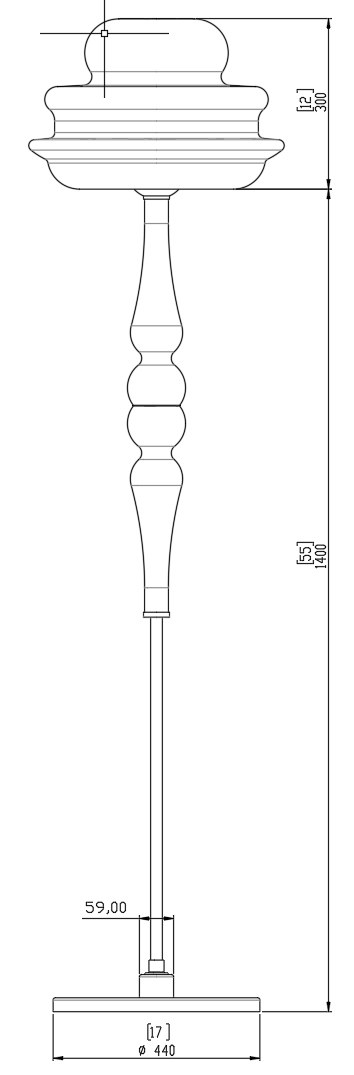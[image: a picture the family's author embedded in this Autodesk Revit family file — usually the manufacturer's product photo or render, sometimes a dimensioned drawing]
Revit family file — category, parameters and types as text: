
# Revit family: PEGGY-Floor
name_source: partatom
category: Lighting Fixtures
units: mm (PartAtom-declared; Revit-internal decimal feet)

## family parameters
Always vertical = Yes
Cut with Voids When Loaded = No
Light Source = No
OmniClass Number = 23.80.70.00
OmniClass Title = Lighting
Part Type = Normal
Room Calculation Point = No
Round Connector Dimension = Use Diameter
Shared = No
Work Plane-Based = Yes

## types (1)
- PEGGY PT
    Bulb Diametr = 15 mm  [stored 0.0492126 ft]
    Country = Europe
    Default Elevation = 1219 mm
    Depth = 28 mm
    Description = FLOOR LAMP
    Designer = Hangar Design Group
    Height = 1400 mm  [stored 4.59318 ft]
    Manufacturer = Vistosi
    Manufacturer country = Italy
    Model = PEGGY
    Type Comments = Hangar Design Group
    URL = https://vistosi.com
    URL Product Page = https://vistosi.it
    Width = 20 mm  [stored 0.0656168 ft]

note: [stored X ft] marks values corroborated as IEEE doubles in the binary element streams (Revit-internal decimal feet)

## geometry (parser evidence)
native form markers: Sweep x6
no freeform markers — native parametric forms only
